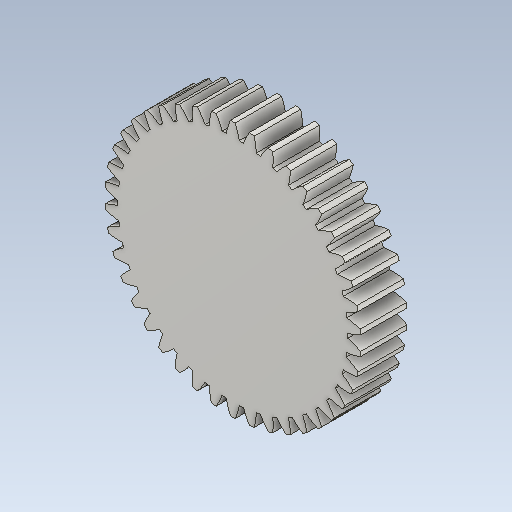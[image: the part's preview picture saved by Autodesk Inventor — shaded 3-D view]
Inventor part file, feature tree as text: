
AUTODESK INVENTOR PART (.ipt)
format: ipt  version: 2020 (Build 240168000, 168)  size: 333,312 bytes
history: native  units: mm (DEFAULTED — no unit token found)
features: plane x3, other x3, sketch x2, extrude x1
ambient origin geometry x8: Origin, YZ Plane, XZ Plane, XY Plane, X Axis, Y Axis, Z Axis, Center Point
bodies: Solid1 (feature_tree)
feature tree (9):
  extrude  "Extrusion1"  Depth=7.6mm TaperAngle=0.0deg
  plane  "Work Plane2"
  plane  "Work Plane8"
  plane  "Work Plane9"
  other  "Przekładnia walcowa"
  sketch  "Sketch1"  dims[d0=41.899531mm d1=7.6mm d2=0.0mm]
  sketch  "Sketch2"  dims[d3=40.0mm d4=10.0mm d5=0.0mm d16=30.0mm d17=0.0mm d34=0.747998mm d39=0.0mm d41=0.0mm d43=30.0mm d46=30.0mm d47=0.0mm d48=0.0mm]
  other  "Srf1"
  other  "Średnica podziałowa"
